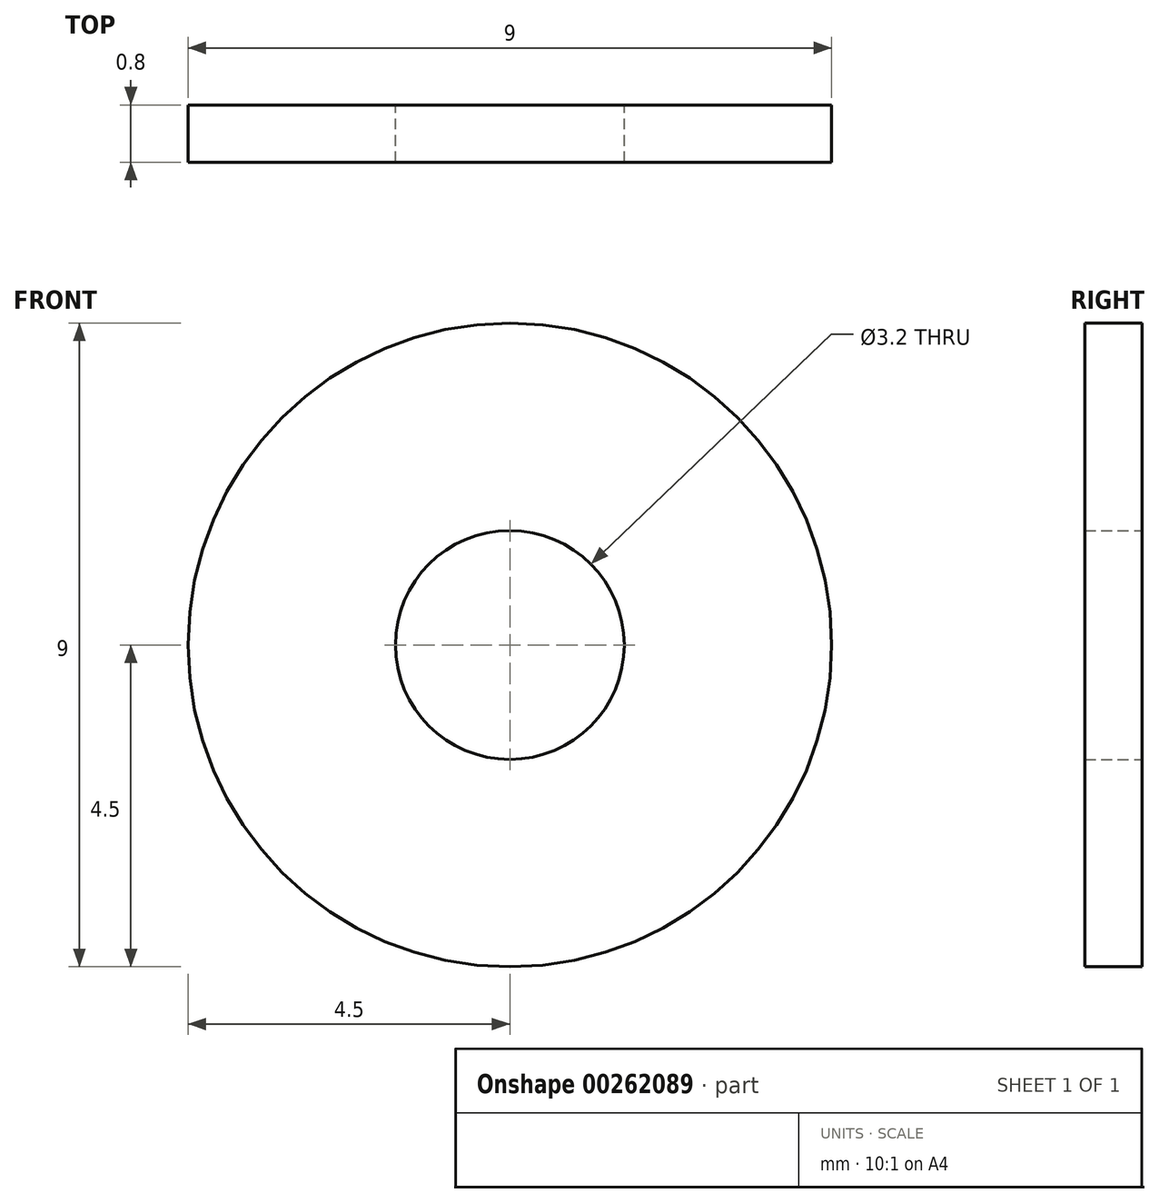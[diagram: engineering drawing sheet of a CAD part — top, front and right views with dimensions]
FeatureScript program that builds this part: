
annotation { "Feature Type Name" : "Feature", "Feature Type Description" : "" }
export const myFeature = defineFeature(function(context is Context, id is Id, definition is map)
    precondition{}
    {
        {
            assignVariable(context, id + "F0", {"name" : "Depth", "anyValue" : .8});
        }
        {
            assignVariable(context, id + "F1", {"name" : "Inner_Diameter", "anyValue" : 3.2});
        }
        {
            assignVariable(context, id + "F2", {"name" : "Di", "anyValue" : getVariable(context, 'Inner_Diameter')});
        }
        {
            var Q0;
            Q0=qCreatedBy(makeId("Front.planeOp"),FACE);
            var sketch = newSketch(context, id + "F3", { "sketchPlane" : qUnion([Q0])});
            skCircle(sketch, "E0", {"center": v(0, 0) * mm, "radius": 4.5 * mm});
            skSolve(sketch);
        }
        {
            var Q0;
            Q0=makeQuery(id+"F3.imprint","IMPRINT",FACE,{"disambiguationData":[TD([[makeQuery(id+"F3.imprint","IMPRINT",EDGE,{"derivedFrom":sQuery(id+"F3.wireOp",EDGE,"E0")}),1.0]])]});
            var Q1;
            Q1=sQuery(id+"F3.wireOp",EDGE,"E0");
            extrude(context, id + "F4", {"entities" : qUnion([Q0]), "surfaceEntities" : qUnion([Q1]), "depth" : (getVariable(context, 'Depth')) * mm});
        }
        {
            var Q0;
            Q0=makeQuery(id+"F4.opExtrude","CAP_FACE",FACE,{"disambiguationData":[OSD([sQuery(id+"F3.wireOp",EDGE,"E0")])],"isStart":false});
            var sketch = newSketch(context, id + "F5", { "sketchPlane" : qUnion([Q0])});
            skPoint(sketch, "E1", {"position": v(0, 0) * mm});
            skSolve(sketch);
        }
        {
            var Q0;
            Q0=sQuery(id+"F5.wireOp",VERTEX,"E1");
            var Q1;
            Q1=makeQuery(id+"F4.opExtrude","SWEPT_BODY",BODY,{"disambiguationData":[OSD([sQuery(id+"F3.wireOp",EDGE,"E0")])]});
            hole(context, id + "F6", {"style" : HoleStyle.SIMPLE, "endStyle" : HoleEndStyle.THROUGH, "holeDiameter" : (getVariable(context, 'Di')) * mm, "locations" : qUnion([Q0]), "scope" : qUnion([Q1]), "isTappedThrough" : true, "startStyle" : HoleStartStyle.PART});
        }
    });
